# Revit family: ISI_IdealStandard_PedestalWashBasins_Tempo-35cm
name_source: partatom
category: Plumbing Fixtures
revit_build: Autodesk Revit MEP 2012 (Build: 20110309_2315(x64)
units: mm (PartAtom-declared; Revit-internal decimal feet)

## types (3) — shared parameters
Accessories = www.idealspec.co.uk
AreaUnits = millimeters
Assembly Code = C1030200
AssetType = Fixed
Brand = Ideal Standard
Category = SanitaryTerminal_WASHHANDBASIN_UK
Color = White
ConnectionType = Plumbing
Default Elevation = 815 mm  [stored 2.67388 ft]
DrainSize = 32 mm  [stored 0.104987 ft]
DurationUnit = year
ECA = No
ExpectedLife = 30
Finish = Colour
IfcExportAs = IfcSanitaryTerminalType
IfcExportType = WASHHANDBASIN
InstallationInstructions = www.idealspec.co.uk/resources.html
LinearUnits = millimeters
ManufacturerURL = www.idealspec.co.uk
Material = Vitreous china
NBSDescription = Pedestal wash basins
NBSReference = 45-35-70/365
NettWeight = 6.5 Kg
NominalDepth = 301 mm
NominalHeight = 815 mm  [stored 2.67388 ft]
NominalLength = 301 mm
NominalWidth = 351 mm
Shape = Sculptured
Size = 350 x 300 x 815 mm
Space = Internal
SpareParts = www.fastpart-spares.co.uk
URL = www.idealspec.co.uk
Uniclass2 = Pr_40_20_96_63
Version = 2
VolumeUnits = Litres
WRAS = No
WarrantyDescription = Manufacturers Warranty
WarrantyDurationParts = 99
WarrantyDurationUnit = year
WashHandBasinMounting = WallHung
WashHandBasinType = HandRinse
WaterEfficientProduct = No
zero-valued in all types: CWFU, HWFU, WFU

## per-type parameters (varying)
| type | 1THLH | 1THRH | 2TH | BIMObjectName | Description | Features | Model | ModelNumber | ModelReference | Name | ProductInformation |
| T059601 - Tempo 35cm handrinse washbasin, 2 tapholes | Yes | Yes | Yes | ISI_IdealStandard_PedestalWashBasins_Tempo-35cm_T0596 | Tempo 35 cm handrinse washbasin, 2 tapholes | 35 cm handrinse washbasin, 2 tapholes | T059601 | T059601 | Tempo 35 cm handrinse washbasin, 2 tapholes | WallHungWashBasins_Tempo-35cm_T0596_IdealStandard | www.idealspec.co.uk/assets/datasheet/T059601 |
| T059701 - Tempo 35cm handrinse washbasin, Right Hand taphole | No | Yes | No | ISI_IdealStandard_PedestalWashBasins_Tempo-35cm_T0597 | Tempo 35 cm handrinse washbasin, right hand tapholes | 35 cm handrinse washbasin, right hand taphole | T059701 | T059701 | Tempo 35 cm handrinse washbasin, right hand tapholes | WallHungWashBasins_Tempo-35cm_T0597_IdealStandard | www.idealspec.co.uk/assets/datasheet/T059701 |
| T059501 - Tempo 35cm handrinse washbasin, Left Hand taphole | Yes | No | No | ISI_IdealStandard_PedestalWashBasins_Tempo-35cm_T0595 | Tempo 35 cm handrinse washbasin, left hand taphole | 35 cm handrinse washbasin, left hand taphole | T059501 | T059501 | Tempo 35 cm handrinse washbasin, left hand taphole | WallHungWashBasins_Tempo-35cm_T0595_IdealStandard | www.idealspec.co.uk/assets/datasheet/T059501 |

note: [stored X ft] marks values corroborated as IEEE doubles in the binary element streams (Revit-internal decimal feet)

## geometry (parser evidence)
native form markers: Blend x2, Sweep x15
no freeform markers — native parametric forms only
